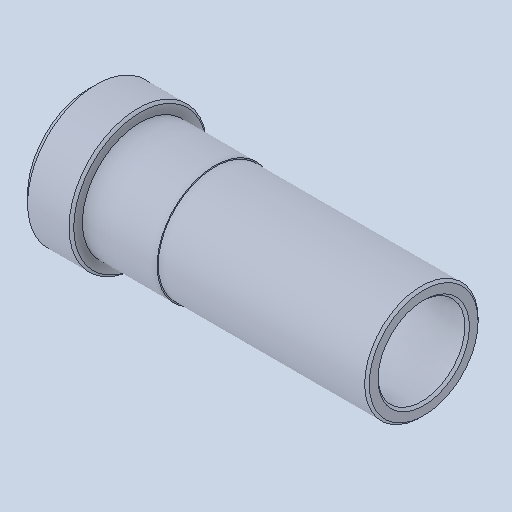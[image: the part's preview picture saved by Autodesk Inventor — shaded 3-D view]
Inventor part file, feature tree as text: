
AUTODESK INVENTOR PART (.ipt)
format: ipt  version: 2023.4 (Build 274418000, 418)  size: 135,680 bytes
history: native  units: in
note: dims shown in document units (in); Inventor stores cm internally (conversion verified against a paired STEP export)
features: chamfer x1
ambient origin geometry x8: Origin, YZ Plane, XZ Plane, XY Plane, X Axis, Y Axis, Z Axis, Center Point
bodies: Solid1 (feature_tree)
feature tree (1):
  chamfer  "Chamfer3"  [1 undecoded]
note: 1 required parameter value undecoded (feature->parameter linkage not recoverable at this tier; creation-order binding heuristic only, values carry confidence <= 0.55)
